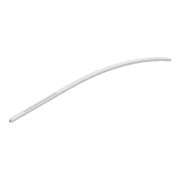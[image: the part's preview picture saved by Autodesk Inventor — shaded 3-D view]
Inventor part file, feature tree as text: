
AUTODESK INVENTOR PART (.ipt)
format: ipt  version: 2022 (Build 260153000, 153)  size: 123,904 bytes
history: native  units: mm
features: extrude x2, sketch x2, projected_geometry x2, fillet x1
ambient origin geometry x8: Origin, YZ Plane, XZ Plane, XY Plane, X Axis, Y Axis, Z Axis, Center Point
bodies: Solid1 (feature_tree)
feature tree (7):
  extrude  "Extrusion1"  Depth=10.0mm
  extrude  "Extrusion2"  Depth=2.0mm
  fillet  "Fillet1"  Radius=140.0mm
  sketch  "Sketch1"  dims[d0=180.0mm d1=10.0mm]
  sketch  "Sketch2"  dims[d2=3.3mm d3=40.0mm d5=140.0mm d6=3.3mm d7=6.0mm d8=0.0mm d9=6.0mm d10=498.004mm d11=90.0mm d12=10.0mm d13=0.0mm d14=2.0mm]
  projected_geometry  "Projected Loop1"
  projected_geometry  "Projected Loop2"
